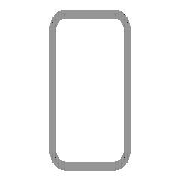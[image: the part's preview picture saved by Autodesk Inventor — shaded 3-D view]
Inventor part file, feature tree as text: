
AUTODESK INVENTOR PART (.ipt)
format: ipt  version: 2025 (Build 290162010, 162A)  size: 133,632 bytes
history: native  units: mm (DEFAULTED — no unit token found)
features: other x4, sketch x1, plane x1
ambient origin geometry x8: Origin, YZ Plane, XZ Plane, XY Plane, X Axis, Y Axis, Z Axis, Center Point
bodies: Solid1 (feature_tree), Body (feature_tree)
feature tree (6):
  parser-record x1  (decoder bookkeeping rows leaked as tree rows — omitted from the tree; the rows remain in map.json)
  other  "Driven Length"
  other  "Start Plane"
  other  "End Plane"
  sketch  "Sketch3"  dims[d3=720.0mm d4=0.0mm d7=6.0mm d9=40.0mm d11=60.0mm d12=3.0mm d13=40.0mm d14=760.0mm d15=20.0mm d16=30.0mm d17=90.0deg d18=720.0mm]
  plane  "Work Plane3"
